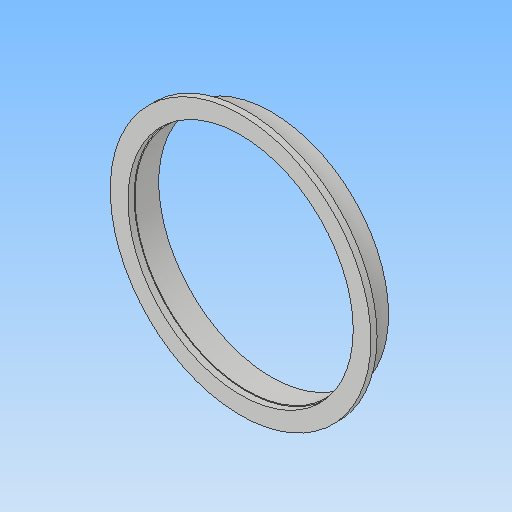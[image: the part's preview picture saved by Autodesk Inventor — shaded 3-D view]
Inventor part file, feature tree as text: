
AUTODESK INVENTOR PART (.ipt)
format: ipt  version: 2019.4 (Build 234330000, 330)  size: 130,048 bytes
history: native  units: mm
features: extrude x2, sketch x1, plane x1
ambient origin geometry x8: Origin, YZ Plane, XZ Plane, XY Plane, X Axis, Y Axis, Z Axis, Center Point
bodies: Solid1 (feature_tree)
feature tree (4):
  sketch  "Sketch1"  dims[d2=4.0mm d3=-0.349066mm d5=2.0mm d6=1.0mm d7=0.0mm d14=38.2mm d16=2.0mm d17=1.0mm]
  plane  "Work Plane1"
  extrude  "Extrusion1"  Depth=1.0mm
  extrude  "Extrusion2"  Depth=1.0mm TaperAngle=0.0deg
